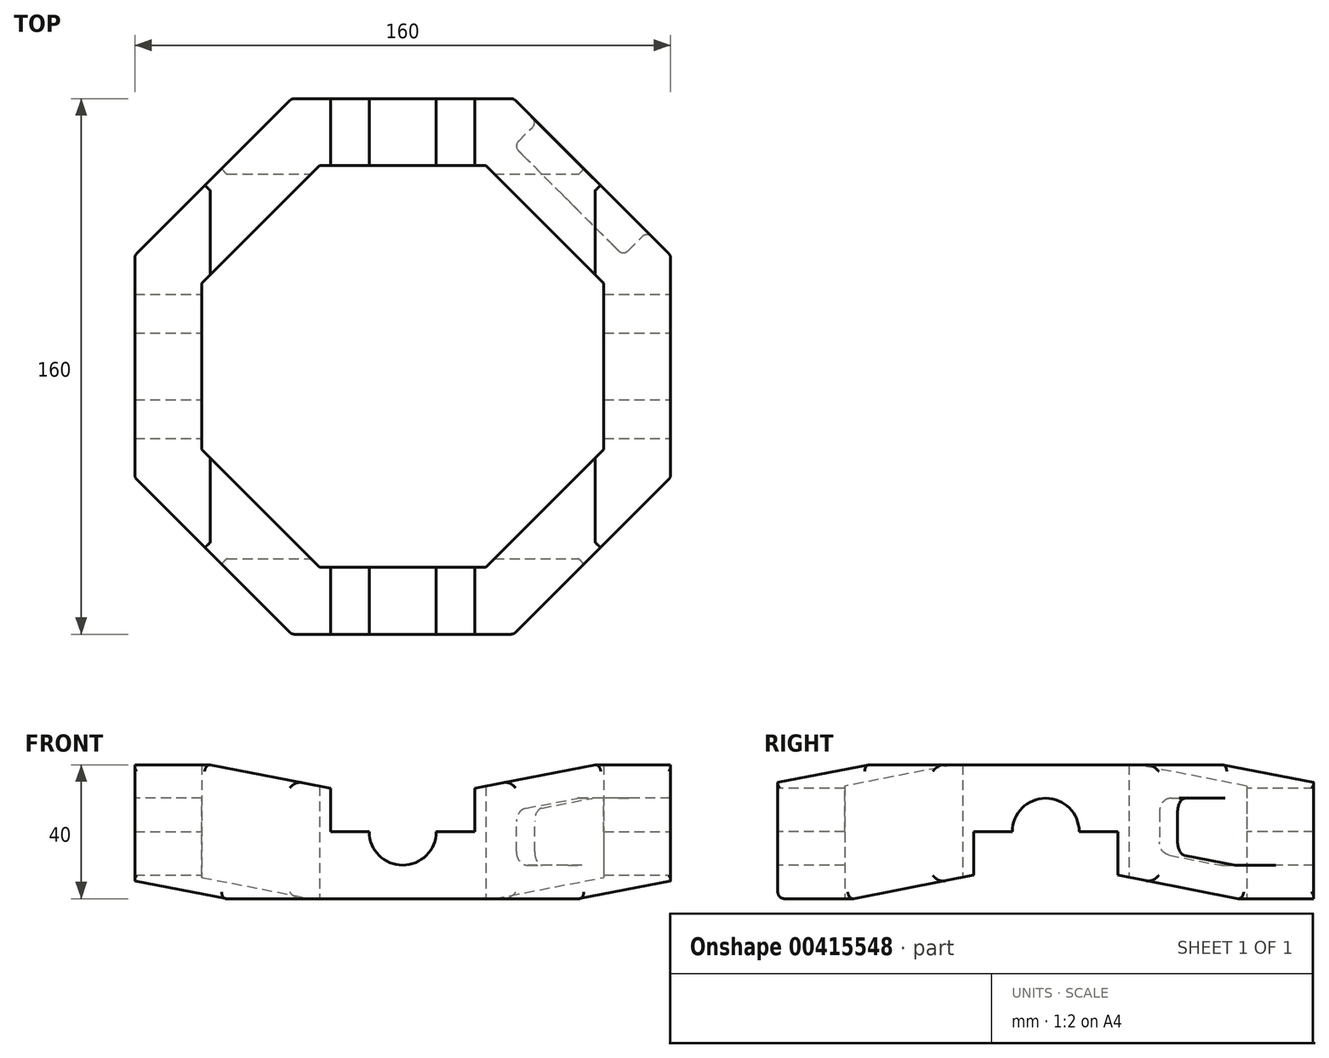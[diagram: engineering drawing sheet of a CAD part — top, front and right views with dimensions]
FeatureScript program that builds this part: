
annotation { "Feature Type Name" : "Feature", "Feature Type Description" : "" }
export const myFeature = defineFeature(function(context is Context, id is Id, definition is map)
    precondition{}
    {
        {
            var Q0;
            Q0=qCreatedBy(makeId("Top.planeOp"),FACE);
            var sketch = newSketch(context, id + "F0", { "sketchPlane" : qUnion([Q0])});
            skCircle(sketch, "E0.cCircle", {"center": v(0, 0) * mm, "radius": 80 * mm, "construction": true});
            skLineSegment(sketch, "E0.0", {"start": v(33.14, -80) * mm, "end": v(-33.14, -80) * mm});
            skLineSegment(sketch, "E0.2", {"start": v(-80, -33.14) * mm, "end": v(-80, 33.14) * mm});
            skLineSegment(sketch, "E0.4", {"start": v(-33.14, 80) * mm, "end": v(33.14, 80) * mm});
            skLineSegment(sketch, "E0.6", {"start": v(80, 33.14) * mm, "end": v(80, -33.14) * mm});
            skPoint(sketch, "E0.0.midPoint", {"position": v(0, -80) * mm});
            skCircle(sketch, "E1.cCircle", {"center": v(0, 0) * mm, "radius": 60 * mm, "construction": true});
            skLineSegment(sketch, "E1.0", {"start": v(24.85, -60) * mm, "end": v(-24.85, -60) * mm});
            skLineSegment(sketch, "E1.2", {"start": v(-60, -24.85) * mm, "end": v(-60, 24.85) * mm});
            skLineSegment(sketch, "E1.4", {"start": v(-24.85, 60) * mm, "end": v(24.85, 60) * mm});
            skLineSegment(sketch, "E1.6", {"start": v(60, 24.85) * mm, "end": v(60, -24.85) * mm});
            skPoint(sketch, "E1.0.midPoint", {"position": v(0, -60) * mm});
            skArc(sketch, "E2", {"start": v(60, -24.85) * mm, "mid": v(49.7, -49.7) * mm, "end": v(24.85, -60) * mm, "construction": true});
            skArc(sketch, "E3", {"start": v(80, -33.14) * mm, "mid": v(66.27, -66.27) * mm, "end": v(33.14, -80) * mm, "construction": true});
            skArc(sketch, "E4", {"start": v(-33.14, -80) * mm, "mid": v(-66.27, -66.27) * mm, "end": v(-80, -33.14) * mm, "construction": true});
            skArc(sketch, "E5", {"start": v(-24.85, -60) * mm, "mid": v(-49.7, -49.7) * mm, "end": v(-60, -24.85) * mm, "construction": true});
            skArc(sketch, "E6", {"start": v(-60, 24.85) * mm, "mid": v(-49.7, 49.7) * mm, "end": v(-24.85, 60) * mm, "construction": true});
            skArc(sketch, "E7", {"start": v(-80, 33.14) * mm, "mid": v(-66.27, 66.27) * mm, "end": v(-33.14, 80) * mm, "construction": true});
            skArc(sketch, "E8", {"start": v(60, 24.85) * mm, "mid": v(49.7, 49.7) * mm, "end": v(24.85, 60) * mm, "construction": true});
            skArc(sketch, "E9", {"start": v(80, 33.14) * mm, "mid": v(66.27, 66.27) * mm, "end": v(33.14, 80) * mm, "construction": true});
            skLineSegment(sketch, "E10", {"start": v(80, 33.14) * mm, "end": v(60, 33.14) * mm, "construction": true});
            skLineSegment(sketch, "E11", {"start": v(60, 33.14) * mm, "end": v(60, 24.85) * mm, "construction": true});
            skLineSegment(sketch, "E12", {"start": v(80, -33.14) * mm, "end": v(60, -33.14) * mm, "construction": true});
            skLineSegment(sketch, "E13", {"start": v(60, -33.14) * mm, "end": v(60, -24.85) * mm, "construction": true});
            skLineSegment(sketch, "E14", {"start": v(33.14, 80) * mm, "end": v(33.14, 60) * mm, "construction": true});
            skLineSegment(sketch, "E15", {"start": v(33.14, 60) * mm, "end": v(24.85, 60) * mm, "construction": true});
            skLineSegment(sketch, "E16", {"start": v(24.85, -60) * mm, "end": v(33.14, -60) * mm, "construction": true});
            skLineSegment(sketch, "E17", {"start": v(33.14, -60) * mm, "end": v(33.14, -80) * mm, "construction": true});
            skArc(sketch, "E18", {"start": v(60, 33.14) * mm, "mid": v(52.13, 52.13) * mm, "end": v(33.14, 60) * mm, "construction": true});
            skArc(sketch, "E19", {"start": v(60, -33.14) * mm, "mid": v(52.13, -52.13) * mm, "end": v(33.14, -60) * mm, "construction": true});
            skLineSegment(sketch, "E20", {"start": v(-80, 33.14) * mm, "end": v(-60, 33.14) * mm, "construction": true});
            skLineSegment(sketch, "E21", {"start": v(-60, 33.14) * mm, "end": v(-60, 24.85) * mm, "construction": true});
            skLineSegment(sketch, "E22", {"start": v(-24.85, 60) * mm, "end": v(-33.14, 60) * mm, "construction": true});
            skLineSegment(sketch, "E23", {"start": v(-33.14, 60) * mm, "end": v(-33.14, 80) * mm, "construction": true});
            skLineSegment(sketch, "E24", {"start": v(-80, -33.14) * mm, "end": v(-60, -33.14) * mm, "construction": true});
            skLineSegment(sketch, "E25", {"start": v(-60, -33.14) * mm, "end": v(-60, -24.85) * mm, "construction": true});
            skLineSegment(sketch, "E26", {"start": v(-24.85, -60) * mm, "end": v(-33.14, -60) * mm, "construction": true});
            skLineSegment(sketch, "E27", {"start": v(-33.14, -60) * mm, "end": v(-33.14, -80) * mm, "construction": true});
            skArc(sketch, "E28", {"start": v(-33.14, -60) * mm, "mid": v(-52.13, -52.13) * mm, "end": v(-60, -33.14) * mm, "construction": true});
            skArc(sketch, "E29", {"start": v(-60, 33.14) * mm, "mid": v(-52.13, 52.13) * mm, "end": v(-33.14, 60) * mm, "construction": true});
            skLineSegment(sketch, "E30", {"start": v(-60, -24.85) * mm, "end": v(-24.85, -60) * mm});
            skLineSegment(sketch, "E31", {"start": v(-80, -33.14) * mm, "end": v(-33.14, -80) * mm});
            skLineSegment(sketch, "E32", {"start": v(24.85, -60) * mm, "end": v(60, -24.85) * mm});
            skLineSegment(sketch, "E33", {"start": v(33.14, -80) * mm, "end": v(80, -33.14) * mm});
            skLineSegment(sketch, "E34", {"start": v(80, 33.14) * mm, "end": v(33.14, 80) * mm});
            skLineSegment(sketch, "E35", {"start": v(60, 24.85) * mm, "end": v(24.85, 60) * mm});
            skLineSegment(sketch, "E36", {"start": v(-24.85, 60) * mm, "end": v(-60, 24.85) * mm});
            skLineSegment(sketch, "E37", {"start": v(-33.14, 80) * mm, "end": v(-80, 33.14) * mm});
            skSolve(sketch);
        }
        {
            var Q0;
            Q0=qSketchRegion(id+"F0",true);
            extrude(context, id + "F1", {"entities" : qUnion([Q0]), "depth" : 40 * mm});
        }
        {
            var Q0;
            Q0=makeQuery(id+"F1.opExtrude","SWEPT_FACE",FACE,{"disambiguationData":[OSD([sQuery(id+"F0.wireOp",EDGE,"E0.0")])]});
            var sketch = newSketch(context, id + "F2", { "sketchPlane" : qUnion([Q0])});
            skCircle(sketch, "E38", {"center": v(0, 20) * mm, "radius": 10 * mm});
            skPoint(sketch, "E38.centerSnap0", {"position": v(0, 0) * mm});
            skSolve(sketch);
        }
        {
            var Q0;
            Q0=qSketchRegion(id+"F2",true);
            extrude(context, id + "F3", {"entities" : qUnion([Q0]), "operationType" : NewBodyOperationType.REMOVE, "oppositeDirection" : true, "depth" : 180 * mm, "hasSecondDirection" : true, "secondDirectionOppositeDirection" : false, "secondDirectionDepth" : 20 * mm});
        }
        {
            var Q0;
            Q0=makeQuery(id+"F1.opExtrude","SWEPT_FACE",FACE,{"disambiguationData":[OSD([sQuery(id+"F0.wireOp",EDGE,"E0.6")])]});
            var sketch = newSketch(context, id + "F4", { "sketchPlane" : qUnion([Q0])});
            skCircle(sketch, "E39", {"center": v(0, 20) * mm, "radius": 10 * mm});
            skSolve(sketch);
        }
        {
            var Q0;
            Q0=qSketchRegion(id+"F4",true);
            extrude(context, id + "F5", {"entities" : qUnion([Q0]), "operationType" : NewBodyOperationType.REMOVE, "depth" : 20 * mm, "hasSecondDirection" : true, "secondDirectionOppositeDirection" : true, "secondDirectionDepth" : 180 * mm});
        }
        {
            var Q0;
            Q0=makeQuery(id+"F1.opExtrude","SWEPT_FACE",FACE,{"disambiguationData":[OSD([sQuery(id+"F0.wireOp",EDGE,"E0.0")])]});
            var sketch = newSketch(context, id + "F6", { "sketchPlane" : qUnion([Q0])});
            skLineSegment(sketch, "E40", {"start": v(0, 0) * mm, "end": v(0, 72.13) * mm, "construction": true});
            skLineSegment(sketch, "E41", {"start": v(0, 20) * mm, "end": v(-21.5, 20) * mm});
            skLineSegment(sketch, "E42", {"start": v(-21.5, 33) * mm, "end": v(-57.5, 40) * mm});
            skLineSegment(sketch, "E43", {"start": v(-57.5, 40) * mm, "end": v(-57.5, 51.7) * mm, "construction": true});
            skLineSegment(sketch, "E44", {"start": v(-57.5, 51.7) * mm, "end": v(0, 51.7) * mm});
            skLineSegment(sketch, "E45", {"start": v(0, 51.7) * mm, "end": v(0, 20) * mm});
            skLineSegment(sketch, "E46.MirrorCS", {"start": v(0, 20) * mm, "end": v(21.5, 20) * mm});
            skLineSegment(sketch, "E47.MirrorCS", {"start": v(21.5, 33) * mm, "end": v(57.5, 40) * mm});
            skLineSegment(sketch, "E48.MirrorCS", {"start": v(57.5, 51.7) * mm, "end": v(0, 51.7) * mm});
            skPoint(sketch, "E49.orphan", {"position": v(22.14, 33.12) * mm});
            skPoint(sketch, "E50.orphan", {"position": v(25, 20) * mm});
            skLineSegment(sketch, "E51", {"start": v(-57.5, 40) * mm, "end": v(-71.93, 40) * mm});
            skLineSegment(sketch, "E52", {"start": v(-71.93, 40) * mm, "end": v(-71.93, 52.97) * mm});
            skLineSegment(sketch, "E53", {"start": v(-71.93, 52.97) * mm, "end": v(-57.5, 51.7) * mm});
            skPoint(sketch, "E54.visualSharp", {"position": v(-57.5, 40) * mm});
            skLineSegment(sketch, "E55.MirrorCS", {"start": v(57.5, 40) * mm, "end": v(57.5, 40) * mm});
            skLineSegment(sketch, "E56.MirrorCS", {"start": v(57.5, 40) * mm, "end": v(71.93, 40) * mm});
            skLineSegment(sketch, "E57.MirrorCS", {"start": v(71.93, 40) * mm, "end": v(71.93, 52.97) * mm});
            skLineSegment(sketch, "E58.MirrorCS", {"start": v(71.93, 52.97) * mm, "end": v(57.5, 51.7) * mm});
            skPoint(sketch, "E59.orphan", {"position": v(57.5, 40) * mm});
            skLineSegment(sketch, "E60", {"start": v(-21, 20) * mm, "end": v(-21, 33) * mm, "construction": true});
            skLineSegment(sketch, "E61", {"start": v(-21, 33) * mm, "end": v(0, 33) * mm, "construction": true});
            skLineSegment(sketch, "E62", {"start": v(-19, 33) * mm, "end": v(-19, 28) * mm, "construction": true});
            skLineSegment(sketch, "E63", {"start": v(-19, 28) * mm, "end": v(-15, 28) * mm, "construction": true});
            skLineSegment(sketch, "E64", {"start": v(-15, 28) * mm, "end": v(-15, 36.1) * mm, "construction": true});
            skLineSegment(sketch, "E65", {"start": v(-15, 36.1) * mm, "end": v(-15, 16.64) * mm, "construction": true});
            skLineSegment(sketch, "E66", {"start": v(-17.5, 28) * mm, "end": v(-17.5, 20) * mm, "construction": true});
            skPoint(sketch, "E67.start.orphan", {"position": v(-11, 28) * mm});
            skLineSegment(sketch, "E68.MirrorCS", {"start": v(-11, 33) * mm, "end": v(-11, 28) * mm, "construction": true});
            skLineSegment(sketch, "E69.MirrorCS", {"start": v(-12.5, 28) * mm, "end": v(-12.5, 20) * mm, "construction": true});
            skLineSegment(sketch, "E70.MirrorCS", {"start": v(-11, 28) * mm, "end": v(-15, 28) * mm, "construction": true});
            skLineSegment(sketch, "E71", {"start": v(-21.5, 20) * mm, "end": v(-21.5, 33) * mm});
            skLineSegment(sketch, "E72.MirrorCS", {"start": v(21.5, 20) * mm, "end": v(21.5, 33) * mm});
            skPoint(sketch, "E73.orphan", {"position": v(26.66, 34) * mm});
            skSolve(sketch);
        }
        {
            var Q0;
            {var subQ4=sQuery(id+"F6.wireOp",EDGE,"E42");var subQ10=sQuery(id+"F6.wireOp",EDGE,"E41");var subQ11=makeQuery(id+"F6.imprint","INTERSECT",VERTEX,{"derivedFrom":[subQ10,subQ4]});Q0=makeQuery(id+"F6.imprint","IMPRINT",FACE,{"disambiguationData":[TD([[makeQuery(id+"F6.imprint","IMPRINT",EDGE,{"disambiguationData":[TD([[subQ11,1.0]])],"derivedFrom":subQ10}),-1.0]])]});}
            var Q1;
            {var subQ5=sQuery(id+"F6.wireOp",EDGE,"E43");Q1=makeQuery(id+"F6.imprint","IMPRINT",FACE,{"disambiguationData":[TD([[makeQuery(id+"F6.imprint","IMPRINT",EDGE,{"derivedFrom":subQ5}),-1.0]])]});}
            var Q2;
            {var subQ1=sQuery(id+"F6.wireOp",EDGE,"7ac94bee-ac53-4392-91bc-958311d5dd120.MirrorCS");Q2=makeQuery(id+"F6.imprint","IMPRINT",FACE,{"disambiguationData":[TD([[makeQuery(id+"F6.imprint","IMPRINT",EDGE,{"derivedFrom":subQ1}),1.0]])]});}
            var Q3;
            {var subQ3=sQuery(id+"F0.wireOp",EDGE,"E0.0");var subQ8=makeQuery(id+"F1.opExtrude","CAP_EDGE",EDGE,{"disambiguationData":[OSD([subQ3])],"isStart":false});var subQ10=sQuery(id+"F6.wireOp",EDGE,"E45");var subQ11=makeQuery(id+"F6.imprint","INTERSECT",VERTEX,{"derivedFrom":[subQ8,subQ10]});Q3=makeQuery(id+"F6.imprint","IMPRINT",FACE,{"disambiguationData":[TD([[makeQuery(id+"F6.imprint","IMPRINT",EDGE,{"disambiguationData":[TD([[subQ11,-1.0]])],"derivedFrom":subQ10}),1.0]])]});}
            var Q4;
            {var subQ0=sQuery(id+"F6.wireOp",EDGE,"dbaf1f0e-c584-4a20-9316-590b7c40fa94.filletArc");Q4=makeQuery(id+"F6.imprint","IMPRINT",FACE,{"disambiguationData":[TD([[makeQuery(id+"F6.imprint","IMPRINT",EDGE,{"derivedFrom":subQ0}),1.0]])]});}
            var Q5;
            {var subQ0=sQuery(id+"F6.wireOp",EDGE,"E44");Q5=makeQuery(id+"F6.imprint","IMPRINT",FACE,{"disambiguationData":[TD([[makeQuery(id+"F6.imprint","IMPRINT",EDGE,{"derivedFrom":subQ0}),-1.0]])]});}
            var Q6;
            {var subQ1=sQuery(id+"F6.wireOp",EDGE,"E48.MirrorCS");Q6=makeQuery(id+"F6.imprint","IMPRINT",FACE,{"disambiguationData":[TD([[makeQuery(id+"F6.imprint","IMPRINT",EDGE,{"derivedFrom":subQ1}),1.0]])]});}
            var Q7;
            {var subQ5=sQuery(id+"F6.wireOp",EDGE,"E71");Q7=makeQuery(id+"F6.imprint","IMPRINT",FACE,{"disambiguationData":[TD([[makeQuery(id+"F6.imprint","IMPRINT",EDGE,{"derivedFrom":subQ5}),-1.0]])]});}
            extrude(context, id + "F7", {"entities" : qUnion([Q0, Q1, Q2, Q3, Q4, Q5, Q6, Q7]), "operationType" : NewBodyOperationType.REMOVE, "oppositeDirection" : true, "depth" : 181.4 * mm});
        }
        {
            var Q0;
            Q0=makeQuery(id+"F1.opExtrude","SWEPT_FACE",FACE,{"disambiguationData":[OSD([sQuery(id+"F0.wireOp",EDGE,"E0.6")])]});
            var sketch = newSketch(context, id + "F8", { "sketchPlane" : qUnion([Q0])});
            skLineSegment(sketch, "E74", {"start": v(0, -9.3) * mm, "end": v(0, 63.42) * mm, "construction": true});
            skLineSegment(sketch, "E75", {"start": v(0, 20) * mm, "end": v(-21.5, 20) * mm});
            skPoint(sketch, "E75.endSnap0", {"position": v(33.14, 20) * mm});
            skLineSegment(sketch, "E76", {"start": v(-21.5, 7) * mm, "end": v(-57.5, 0) * mm});
            skLineSegment(sketch, "E77", {"start": v(-57.5, -11.1) * mm, "end": v(0, -11.1) * mm});
            skLineSegment(sketch, "E78", {"start": v(0, -11.1) * mm, "end": v(0, 20) * mm});
            skLineSegment(sketch, "E79.MirrorCS", {"start": v(0, 20) * mm, "end": v(21.5, 20) * mm});
            skLineSegment(sketch, "E80.MirrorCS", {"start": v(21.5, 7) * mm, "end": v(57.5, 0) * mm});
            skLineSegment(sketch, "E81.MirrorCS", {"start": v(57.5, 0) * mm, "end": v(57.5, -11.1) * mm, "construction": true});
            skLineSegment(sketch, "E82.MirrorCS", {"start": v(57.5, -11.1) * mm, "end": v(0, -11.1) * mm});
            skLineSegment(sketch, "E83", {"start": v(21.5, 7) * mm, "end": v(0, 7) * mm, "construction": true});
            skLineSegment(sketch, "E84", {"start": v(21.5, 20) * mm, "end": v(21.5, 7) * mm});
            skLineSegment(sketch, "E85.MirrorCS", {"start": v(-21.5, 20) * mm, "end": v(-21.5, 7) * mm});
            skLineSegment(sketch, "E86", {"start": v(57.5, 0) * mm, "end": v(66.67, 0) * mm});
            skLineSegment(sketch, "E87", {"start": v(66.67, 0) * mm, "end": v(66.67, -11.89) * mm});
            skLineSegment(sketch, "E88", {"start": v(66.67, -11.89) * mm, "end": v(57.5, -11.1) * mm});
            skPoint(sketch, "E89.visualSharp", {"position": v(57.5, 0) * mm});
            skLineSegment(sketch, "E90.MirrorCS", {"start": v(-57.5, 0) * mm, "end": v(-66.67, 0) * mm});
            skLineSegment(sketch, "E91.MirrorCS", {"start": v(-66.67, 0) * mm, "end": v(-66.67, -11.89) * mm});
            skLineSegment(sketch, "E92.MirrorCS", {"start": v(-66.67, -11.89) * mm, "end": v(-57.5, -11.1) * mm});
            skPoint(sketch, "E93.orphan", {"position": v(-57.5, 0) * mm});
            skSolve(sketch);
        }
        {
            var Q0;
            {var subQ0=sQuery(id+"F8.wireOp",EDGE,"E81.MirrorCS");Q0=makeQuery(id+"F8.imprint","IMPRINT",FACE,{"disambiguationData":[TD([[makeQuery(id+"F8.imprint","IMPRINT",EDGE,{"derivedFrom":subQ0}),-1.0]])]});}
            var Q1;
            {var subQ1=sQuery(id+"F8.wireOp",EDGE,"0c2d71ed-c988-4f1d-bc7d-0120d0bb6d290.MirrorCS");Q1=makeQuery(id+"F8.imprint","IMPRINT",FACE,{"disambiguationData":[TD([[makeQuery(id+"F8.imprint","IMPRINT",EDGE,{"derivedFrom":subQ1}),-1.0]])]});}
            var Q2;
            {var subQ0=sQuery(id+"F8.wireOp",EDGE,"2264c362-575d-479c-8459-3a82115e6452.filletArc");Q2=makeQuery(id+"F8.imprint","IMPRINT",FACE,{"disambiguationData":[TD([[makeQuery(id+"F8.imprint","IMPRINT",EDGE,{"derivedFrom":subQ0}),1.0]])]});}
            var Q3;
            {var subQ5=sQuery(id+"F8.wireOp",EDGE,"2P67hEqB-GFHx-fnHL-FwA6-pxk5i6od99Hl");Q3=makeQuery(id+"F8.imprint","IMPRINT",FACE,{"disambiguationData":[TD([[makeQuery(id+"F8.imprint","IMPRINT",EDGE,{"derivedFrom":subQ5}),1.0]])]});}
            var Q4;
            {var subQ0=sQuery(id+"F8.wireOp",EDGE,"E84");Q4=makeQuery(id+"F8.imprint","IMPRINT",FACE,{"disambiguationData":[TD([[makeQuery(id+"F8.imprint","IMPRINT",EDGE,{"derivedFrom":subQ0}),-1.0]])]});}
            var Q5;
            {var subQ0=sQuery(id+"F8.wireOp",EDGE,"E82.MirrorCS");Q5=makeQuery(id+"F8.imprint","IMPRINT",FACE,{"disambiguationData":[TD([[makeQuery(id+"F8.imprint","IMPRINT",EDGE,{"derivedFrom":subQ0}),-1.0]])]});}
            var Q6;
            {var subQ0=sQuery(id+"F8.wireOp",EDGE,"E85.MirrorCS");Q6=makeQuery(id+"F8.imprint","IMPRINT",FACE,{"disambiguationData":[TD([[makeQuery(id+"F8.imprint","IMPRINT",EDGE,{"derivedFrom":subQ0}),1.0]])]});}
            var Q7;
            {var subQ1=sQuery(id+"F8.wireOp",EDGE,"E77");Q7=makeQuery(id+"F8.imprint","IMPRINT",FACE,{"disambiguationData":[TD([[makeQuery(id+"F8.imprint","IMPRINT",EDGE,{"derivedFrom":subQ1}),1.0]])]});}
            extrude(context, id + "F9", {"entities" : qUnion([Q0, Q1, Q2, Q3, Q4, Q5, Q6, Q7]), "operationType" : NewBodyOperationType.REMOVE, "oppositeDirection" : true, "depth" : 244.2 * mm});
        }
        {
            var Q0;
            Q0=makeQuery(id+"F1.opExtrude","SWEPT_FACE",FACE,{"disambiguationData":[OSD([sQuery(id+"F0.wireOp",EDGE,"E34")])]});
            var sketch = newSketch(context, id + "F10", { "sketchPlane" : qUnion([Q0])});
            skLineSegment(sketch, "E94.0", {"start": v(1.73, 10.04) * mm, "end": v(-19.68, 12.98) * mm});
            skLineSegment(sketch, "E94.1", {"start": v(23.14, 23.06) * mm, "end": v(23.14, 14) * mm});
            skLineSegment(sketch, "E94.2", {"start": v(19.68, 27.02) * mm, "end": v(-1.73, 29.96) * mm});
            skLineSegment(sketch, "E94.3", {"start": v(2.28, 10) * mm, "end": v(19.14, 10) * mm});
            skLineSegment(sketch, "E94.4", {"start": v(-19.14, 30) * mm, "end": v(-2.28, 30) * mm});
            skLineSegment(sketch, "E94.5", {"start": v(-23.14, 26) * mm, "end": v(-23.14, 16.94) * mm});
            skPoint(sketch, "E95.visualSharp", {"position": v(23.14, 10) * mm});
            skArc(sketch, "E95.filletArc", {"start": v(19.14, 10) * mm, "mid": v(21.97, 11.17) * mm, "end": v(23.14, 14) * mm});
            skPoint(sketch, "E96.visualSharp", {"position": v(23.14, 26.54) * mm});
            skArc(sketch, "E96.filletArc", {"start": v(23.14, 23.06) * mm, "mid": v(22.15, 25.68) * mm, "end": v(19.68, 27.02) * mm});
            skPoint(sketch, "E97.visualSharp", {"position": v(-23.14, 30) * mm});
            skArc(sketch, "E97.filletArc", {"start": v(-19.14, 30) * mm, "mid": v(-21.97, 28.83) * mm, "end": v(-23.14, 26) * mm});
            skPoint(sketch, "E98.visualSharp", {"position": v(-23.14, 13.46) * mm});
            skArc(sketch, "E98.filletArc", {"start": v(-23.14, 16.94) * mm, "mid": v(-22.15, 14.32) * mm, "end": v(-19.68, 12.98) * mm});
            skPoint(sketch, "E99.visualSharp", {"position": v(2, 10) * mm});
            skArc(sketch, "E99.filletArc", {"start": v(1.73, 10.04) * mm, "mid": v(2, 10) * mm, "end": v(2.28, 10) * mm});
            skPoint(sketch, "E100.visualSharp", {"position": v(-2, 30) * mm});
            skArc(sketch, "E100.filletArc", {"start": v(-1.73, 29.96) * mm, "mid": v(-2, 30) * mm, "end": v(-2.28, 30) * mm});
            skSolve(sketch);
        }
        {
            var Q0;
            Q0=makeQuery(id+"F10.imprint","IMPRINT",FACE,{"disambiguationData":[TD([[makeQuery(id+"F10.imprint","IMPRINT",EDGE,{"derivedFrom":sQuery(id+"F10.wireOp",EDGE,"E94.0")}),-1.0]])]});
            extrude(context, id + "F11", {"entities" : qUnion([Q0]), "operationType" : NewBodyOperationType.REMOVE, "oppositeDirection" : true, "depth" : 10 * mm});
        }
        {
            var Q0;
            Q0=makeQuery(id+"F11.boolean.opBoolean","COPY",EDGE,{"derivedFrom":makeQuery(id+"F11.opExtrude","CAP_EDGE",EDGE,{"disambiguationData":[OSD([sQuery(id+"F10.wireOp",EDGE,"E94.1")])],"isStart":false})});
            var Q1;
            Q1=makeQuery(id+"F11.boolean.opBoolean","COPY",EDGE,{"derivedFrom":makeQuery(id+"F11.opExtrude","CAP_EDGE",EDGE,{"disambiguationData":[OSD([sQuery(id+"F10.wireOp",EDGE,"E95.filletArc")])],"isStart":false})});
            var Q2;
            Q2=makeQuery(id+"F11.boolean.opBoolean","COPY",EDGE,{"derivedFrom":makeQuery(id+"F11.opExtrude","CAP_EDGE",EDGE,{"disambiguationData":[OSD([sQuery(id+"F10.wireOp",EDGE,"E94.3")])],"isStart":false})});
            fillet(context, id + "F12", {"entities" : qUnion([Q0, Q1, Q2]), "radius" : 2 * mm, "tangentPropagation" : true, "allowEdgeOverflow" : false});
        }
        {
            var Q0;
            Q0=makeQuery(id+"F1.opExtrude","CAP_EDGE",EDGE,{"disambiguationData":[OSD([sQuery(id+"F0.wireOp",EDGE,"E34")])],"isStart":true});
            var Q1;
            Q1=makeQuery(id+"F9.boolean.opBoolean","INTERSECT",EDGE,{"derivedFrom":[makeQuery(id+"F1.opExtrude","SWEPT_FACE",FACE,{"disambiguationData":[OSD([sQuery(id+"F0.wireOp",EDGE,"E34")])]}),makeQuery(id+"F9.opExtrude","SWEPT_FACE",FACE,{"disambiguationData":[OSD([sQuery(id+"F8.wireOp",EDGE,"E80.MirrorCS")])]})]});
            var Q2;
            Q2=makeQuery(id+"F1.opExtrude","SWEPT_FACE",FACE,{"disambiguationData":[OSD([sQuery(id+"F0.wireOp",EDGE,"E34")])]});
            var Q3;
            Q3=makeQuery(id+"F1.opExtrude","SWEPT_FACE",FACE,{"disambiguationData":[OSD([sQuery(id+"F0.wireOp",EDGE,"E33")])]});
            var Q4;
            Q4=makeQuery(id+"F1.opExtrude","CAP_EDGE",EDGE,{"disambiguationData":[OSD([sQuery(id+"F0.wireOp",EDGE,"E0.0")])],"isStart":true});
            var Q5;
            Q5=makeQuery(id+"F7.boolean.opBoolean","COPY",EDGE,{"derivedFrom":makeQuery(id+"F7.opExtrude","CAP_EDGE",EDGE,{"disambiguationData":[OSD([sQuery(id+"F6.wireOp",EDGE,"E47.MirrorCS")])],"isStart":true})});
            var Q6;
            Q6=makeQuery(id+"F1.opExtrude","SWEPT_FACE",FACE,{"disambiguationData":[OSD([sQuery(id+"F0.wireOp",EDGE,"E31")])]});
            var Q7;
            Q7=makeQuery(id+"F1.opExtrude","SWEPT_FACE",FACE,{"disambiguationData":[OSD([sQuery(id+"F0.wireOp",EDGE,"E37")])]});
            fillet(context, id + "F13", {"entities" : qUnion([Q0, Q1, Q2, Q3, Q4, Q5, Q6, Q7]), "radius" : 2 * mm, "tangentPropagation" : true, "allowEdgeOverflow" : false});
        }
    });
